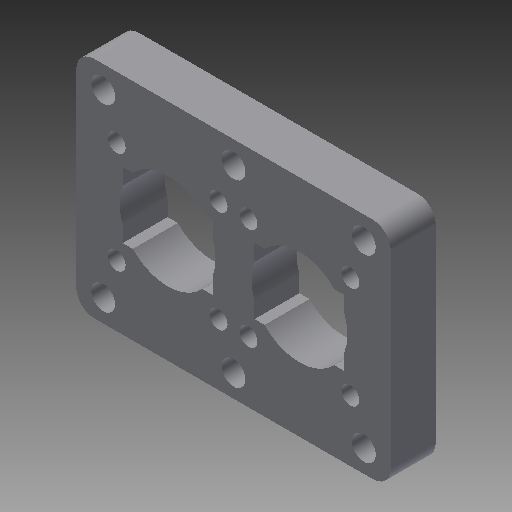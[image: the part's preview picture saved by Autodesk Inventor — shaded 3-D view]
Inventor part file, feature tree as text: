
AUTODESK INVENTOR PART (.ipt)
format: ipt  version: 2017 SP1 (Build 210196100, 196)  size: 181,760 bytes
history: native  units: mm
features: extrude x2, sketch x2, fillet x1
ambient origin geometry x8: Origin, YZ Plane, XZ Plane, XY Plane, X Axis, Y Axis, Z Axis, Center Point
bodies: Solid1 (feature_tree)
feature tree (5):
  extrude  "Extrusion1"  Depth=44.0mm
  fillet  "Fillet1"  Radius=44.0mm
  extrude  "Extrusion2"  Depth=10.0mm
  sketch  "Sketch1"  dims[d0=60.0mm d1=87.0mm d2=44.0mm]
  sketch  "Sketch2"  dims[d3=32.0mm d4=8.0mm d5=105.0mm d6=75.0mm d7=15.0mm d8=0.0mm d9=6.0mm d10=34.0mm d11=6.0mm d12=22.0mm d13=30.0mm d14=10.0mm d15=0.0mm]
